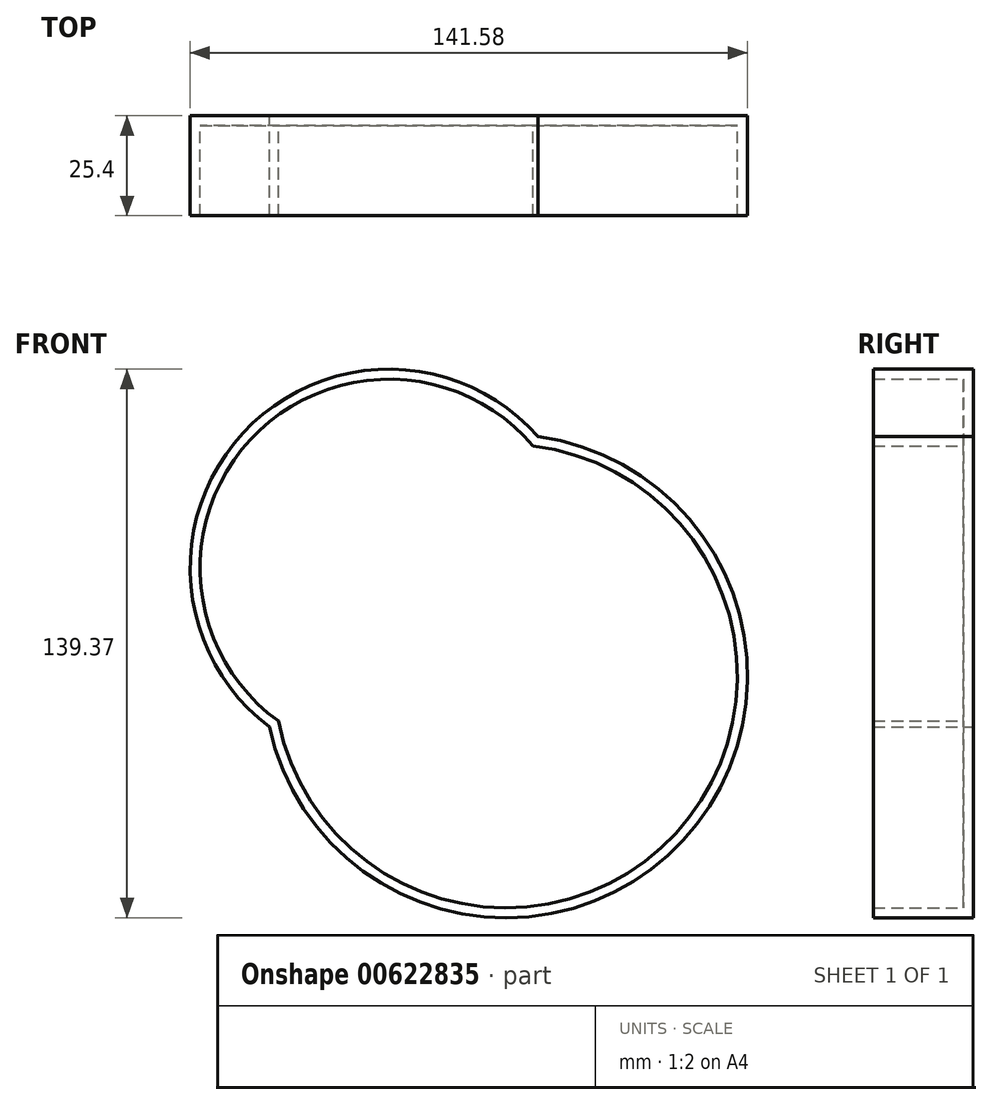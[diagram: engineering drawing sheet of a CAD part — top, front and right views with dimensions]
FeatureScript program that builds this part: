
annotation { "Feature Type Name" : "Feature", "Feature Type Description" : "" }
export const myFeature = defineFeature(function(context is Context, id is Id, definition is map)
    precondition{}
    {
        {
            var Q0;
            Q0=qCreatedBy(makeId("Front.planeOp"),FACE);
            var sketch = newSketch(context, id + "F0", { "sketchPlane" : qUnion([Q0])});
            skArc(sketch, "E0", {"start": v(-19.12, 87.3) * mm, "mid": v(-94.1, 88.23) * mm, "end": v(-87.37, 13.55) * mm});
            skArc(sketch, "E1", {"start": v(-87.37, 13.55) * mm, "mid": v(17.7, -15.25) * mm, "end": v(-19.12, 87.3) * mm});
            skSolve(sketch);
        }
        {
            var Q0;
            Q0 = qSketchRegion(id + "F0", true);
            extrude(context, id + "F1", {"entities" : qUnion([Q0]), "depth" : 25.4 * mm, "offsetDistance" : 25.4 * mm});
        }
        {
            var Q0;
            Q0=makeQuery(id+"F1.opExtrude","CAP_FACE",FACE,{"disambiguationData":[OSD([sQuery(id+"F0.wireOp",EDGE,"E0"),sQuery(id+"F0.wireOp",EDGE,"E1")])],"isStart":false});
            shell(context, id + "F2", {"entities" : qUnion([Q0]), "thickness" : 2.54 * mm});
        }
    });
